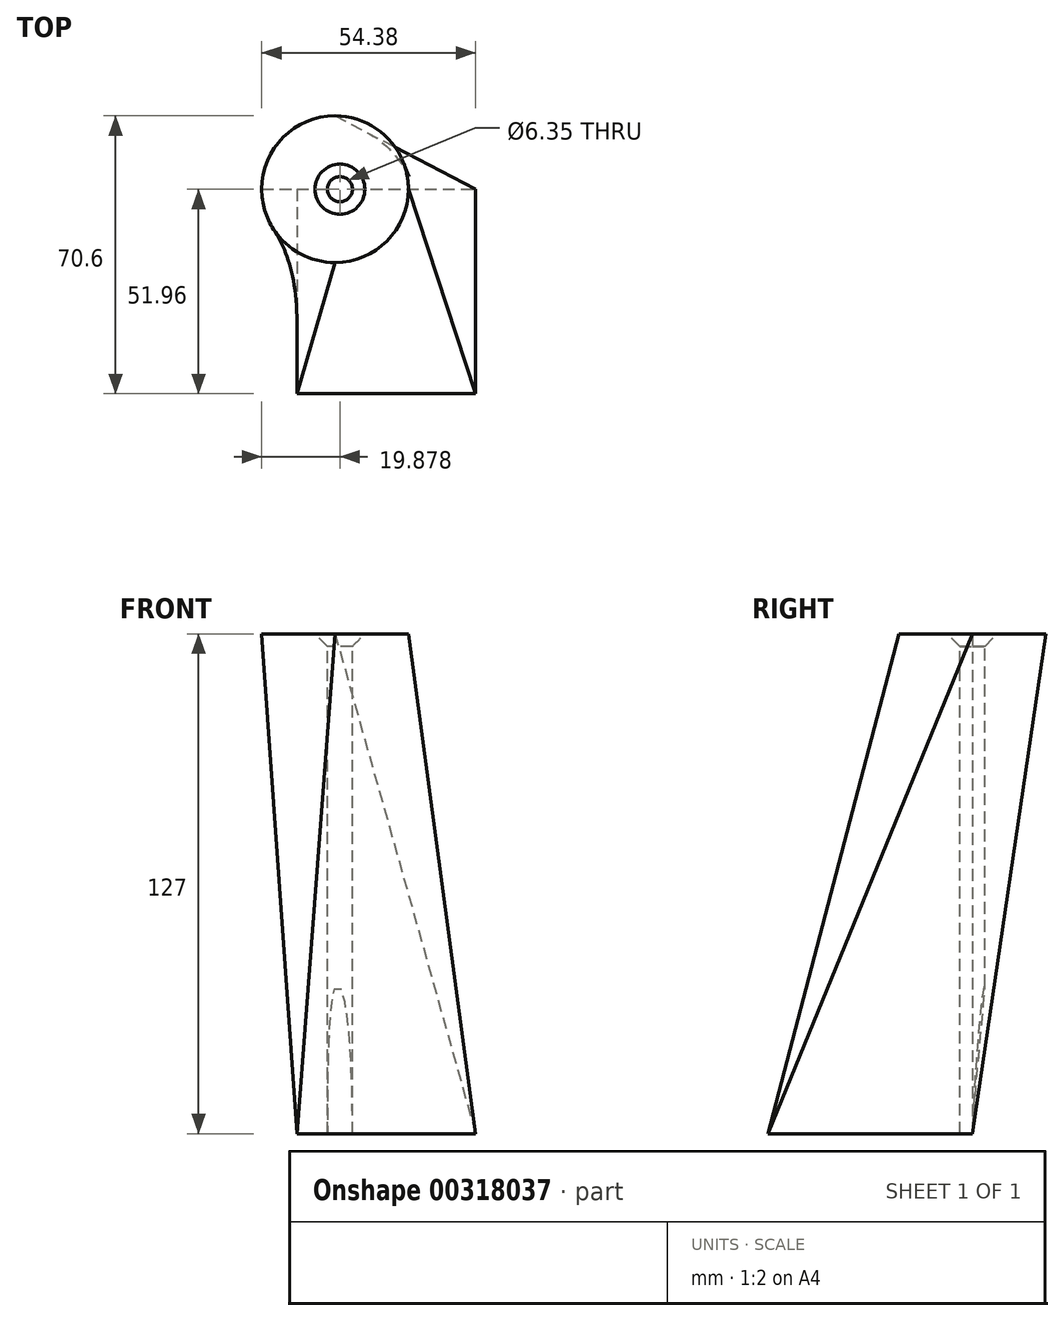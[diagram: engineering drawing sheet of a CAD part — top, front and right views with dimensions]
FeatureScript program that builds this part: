
annotation { "Feature Type Name" : "Feature", "Feature Type Description" : "" }
export const myFeature = defineFeature(function(context is Context, id is Id, definition is map)
    precondition{}
    {
        {
            var Q0;
            Q0=qCreatedBy(makeId("Top.planeOp"),FACE);
            var sketch = newSketch(context, id + "F0", { "sketchPlane" : qUnion([Q0])});
            skLineSegment(sketch, "E0.bottom", {"start": v(0, 0) * mm, "end": v(45.42, 0) * mm});
            skLineSegment(sketch, "E0.top", {"start": v(0, -51.96) * mm, "end": v(45.42, -51.96) * mm});
            skLineSegment(sketch, "E0.left", {"start": v(0, 0) * mm, "end": v(0, -51.96) * mm});
            skLineSegment(sketch, "E0.right", {"start": v(45.42, 0) * mm, "end": v(45.42, -51.96) * mm});
            skSolve(sketch);
        }
        {
            var Q0;
            Q0=qCreatedBy(makeId("Top.planeOp"),FACE);
            cPlane(context, id + "F1", {"entities" : qUnion([Q0]), "cplaneType" : CPlaneType.OFFSET, "offset" : 127 * mm, "width" : 152.4 * mm, "height" : 152.4 * mm});
        }
        {
            var Q0;
            Q0=qCreatedBy(id+"F1.planeOp",FACE);
            var sketch = newSketch(context, id + "F2", { "sketchPlane" : qUnion([Q0])});
            skCircle(sketch, "E1", {"center": v(9.68, 0) * mm, "radius": 18.64 * mm});
            skSolve(sketch);
        }
        {
            var Q0;
            Q0=makeQuery(id+"F2.imprint","IMPRINT",FACE,{"disambiguationData":[TD([[makeQuery(id+"F2.imprint","IMPRINT",EDGE,{"derivedFrom":sQuery(id+"F2.wireOp",EDGE,"E1")}),1.0]])]});
            var Q1;
            Q1=makeQuery(id+"F0.imprint","IMPRINT",FACE,{"disambiguationData":[TD([[makeQuery(id+"F0.imprint","IMPRINT",EDGE,{"derivedFrom":sQuery(id+"F0.wireOp",EDGE,"E0.bottom")}),-1.0]])]});
            loft(context, id + "F3", {"sheetProfilesArray" : [{ "sheetProfileEntities" : qUnion([Q0]) }, { "sheetProfileEntities" : qUnion([Q1]) }]});
        }
        {
            var Q0;
            Q0=makeQuery(id+"F3.opLoft","CAP_FACE",FACE,{"disambiguationData":[OSD([makeQuery(id+"F2.imprint","IMPRINT",FACE,{"disambiguationData":[TD([[makeQuery(id+"F2.imprint","IMPRINT",EDGE,{"derivedFrom":sQuery(id+"F2.wireOp",EDGE,"E1")}),1.0]])]})])],"isStart":true});
            var sketch = newSketch(context, id + "F4", { "sketchPlane" : qUnion([Q0])});
            skCircle(sketch, "E2", {"center": v(10.92, 0) * mm, "radius": 4.87 * mm});
            skSolve(sketch);
        }
        {
            var Q0;
            Q0=sQuery(id+"F4.wireOp",VERTEX,"E2.center");
            var Q1;
            Q1=makeQuery(id+"F3.opLoft","SWEPT_BODY",BODY,{"disambiguationData":[OSD([makeQuery(id+"F0.imprint","IMPRINT",FACE,{"disambiguationData":[TD([[makeQuery(id+"F0.imprint","IMPRINT",EDGE,{"derivedFrom":sQuery(id+"F0.wireOp",EDGE,"E0.bottom")}),-1.0]])]}),makeQuery(id+"F2.imprint","IMPRINT",FACE,{"disambiguationData":[TD([[makeQuery(id+"F2.imprint","IMPRINT",EDGE,{"derivedFrom":sQuery(id+"F2.wireOp",EDGE,"E1")}),1.0]])]})])]});
            hole(context, id + "F5", {"style" : HoleStyle.C_SINK, "endStyle" : HoleEndStyle.THROUGH, "holeDiameter" : 6.35 * mm, "cSinkDiameter" : 12.7 * mm, "cSinkAngle" : 90 * degree, "tappedDepth" : 12.7 * mm, "tapClearance" : 3, "locations" : qUnion([Q0]), "scope" : qUnion([Q1])});
        }
    });
